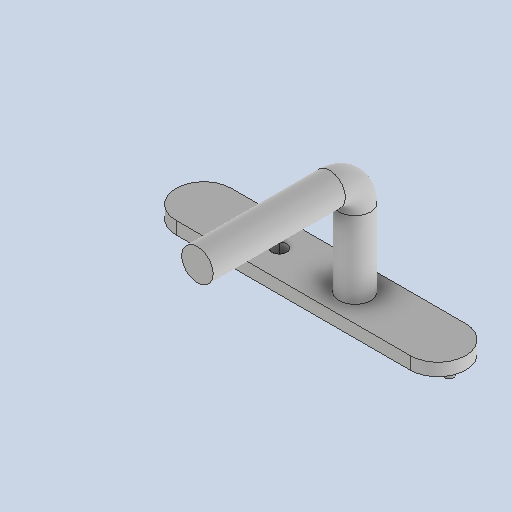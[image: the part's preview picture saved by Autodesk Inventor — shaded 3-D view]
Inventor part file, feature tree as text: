
AUTODESK INVENTOR PART (.ipt)
format: ipt  version: 2025.1 (Build 291241000, 241)  size: 303,104 bytes
history: native  units: mm
features: sketch x5, extrude x3, other x1, plane x1, sweep x1, projected_geometry x1
ambient origin geometry x8: Origin, YZ Plane, XZ Plane, XY Plane, X Axis, Y Axis, Z Axis, Center Point
bodies: Body1 (feature_tree)
feature tree (12):
  sketch  "Sketch1"  dims[d0=25.0mm d1=61.0mm]
  sketch  "Sketch2"  dims[d8=0.0mm d9=0.0mm d10=44.0mm]
  other  "Work Point1"
  plane  "Work Plane1"
  sweep  "Sweep2"
  extrude  "Extrusion1"  Depth=44.0mm
  extrude  "Extrusion2"  Depth=230.0mm
  extrude  "Extrusion3"  Depth=10.0mm
  sketch  "Sketch4"  dims[d12=88.0mm d13=230.0mm]
  projected_geometry  "Projected Loop1"
  sketch  "Sketch5"  dims[d14=10.0mm d15=0.0mm d16=7.0mm]
  sketch  "Sketch6"  dims[d17=21.5mm d18=75.0mm d19=90.5mm d20=10.0mm d21=0.0mm d22=12.0mm d23=60.0mm d24=4.5mm d25=23.0mm d26=10.0mm d27=0.0mm d28=20.0mm d29=105.0mm]
